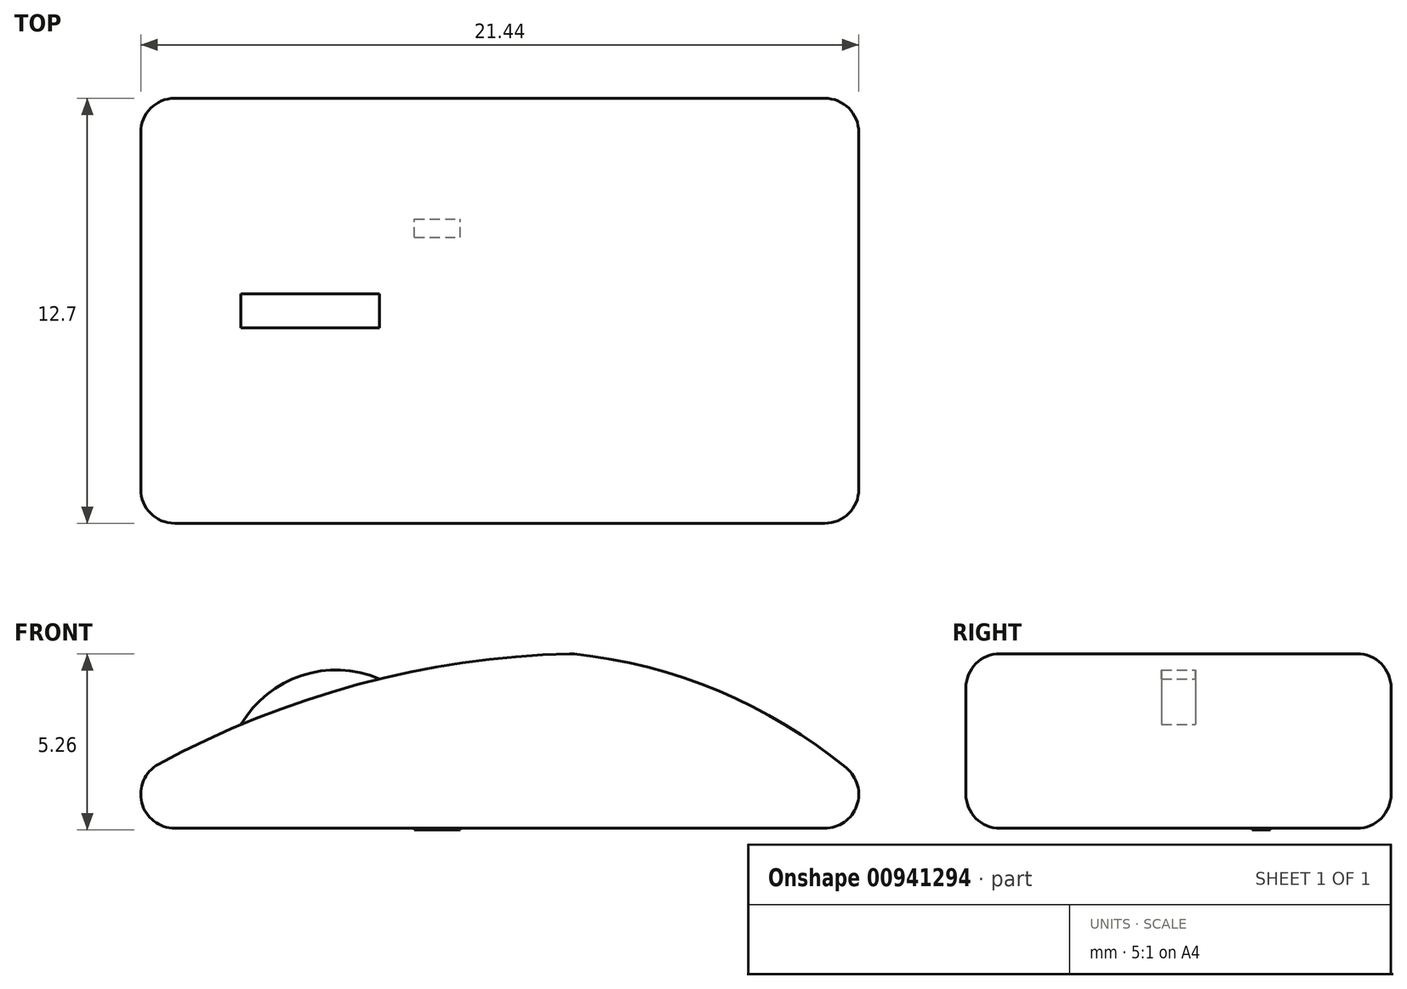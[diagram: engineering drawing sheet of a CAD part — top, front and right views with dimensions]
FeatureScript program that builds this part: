
annotation { "Feature Type Name" : "Feature", "Feature Type Description" : "" }
export const myFeature = defineFeature(function(context is Context, id is Id, definition is map)
    precondition{}
    {
        {
            var Q0;
            Q0=qCreatedBy(makeId("Front.planeOp"),FACE);
            var sketch = newSketch(context, id + "F0", { "sketchPlane" : qUnion([Q0])});
            skLineSegment(sketch, "E0", {"start": v(-53.26, -21) * mm, "end": v(73.74, -21) * mm});
            skArc(sketch, "E1", {"start": v(73.74, -21) * mm, "mid": v(51.12, -3.16) * mm, "end": v(23.51, 5.07) * mm});
            skArc(sketch, "E2", {"start": v(23.51, 5.07) * mm, "mid": v(-16.87, -2.09) * mm, "end": v(-53.26, -21) * mm});
            skArc(sketch, "E3", {"start": v(-5.21, 1.3) * mm, "mid": v(-16.84, 1.81) * mm, "end": v(-25.9, -5.52) * mm});
            skSolve(sketch);
        }
        {
            var Q0;
            {var subQ5=sQuery(id+"F0.wireOp",EDGE,"E0");Q0=makeQuery(id+"F0.imprint","IMPRINT",FACE,{"disambiguationData":[TD([[makeQuery(id+"F0.imprint","IMPRINT",EDGE,{"derivedFrom":subQ5}),1.0]])]});}
            extrude(context, id + "F1", {"entities" : qUnion([Q0]), "depth" : 31.75 * mm, "offsetDistance" : 25.4 * mm, "hasSecondDirection" : true, "secondDirectionOppositeDirection" : true, "secondDirectionDepth" : 31.75 * mm});
        }
        {
            var Q0;
            {var subQ0=sQuery(id+"F0.wireOp",EDGE,"E3");Q0=makeQuery(id+"F0.imprint","IMPRINT",FACE,{"disambiguationData":[TD([[makeQuery(id+"F0.imprint","IMPRINT",EDGE,{"derivedFrom":subQ0}),1.0]])]});}
            extrude(context, id + "F2", {"entities" : qUnion([Q0]), "operationType" : NewBodyOperationType.ADD, "depth" : 2.54 * mm, "offsetDistance" : 25.4 * mm, "hasSecondDirection" : true, "secondDirectionOppositeDirection" : true, "secondDirectionDepth" : 2.54 * mm});
        }
        {
            var Q0;
            Q0=makeQuery(id+"F1.opExtrude","SWEPT_EDGE",EDGE,{"disambiguationData":[OSD([sQuery(id+"F0.wireOp",EDGE,"E0"),sQuery(id+"F0.wireOp",EDGE,"E2")])]});
            var Q1;
            Q1=makeQuery(id+"F1.opExtrude","CAP_FACE",FACE,{"disambiguationData":[OSD([sQuery(id+"F0.wireOp",EDGE,"E0"),sQuery(id+"F0.wireOp",EDGE,"E1"),sQuery(id+"F0.wireOp",EDGE,"E2")])],"isStart":false});
            var Q2;
            Q2=makeQuery(id+"F1.opExtrude","CAP_FACE",FACE,{"disambiguationData":[OSD([sQuery(id+"F0.wireOp",EDGE,"E0"),sQuery(id+"F0.wireOp",EDGE,"E1"),sQuery(id+"F0.wireOp",EDGE,"E2")])],"isStart":true});
            var Q3;
            Q3=makeQuery(id+"F1.opExtrude","SWEPT_FACE",FACE,{"disambiguationData":[OSD([sQuery(id+"F0.wireOp",EDGE,"E1")])]});
            var Q4;
            Q4=makeQuery(id+"F1.opExtrude","SWEPT_EDGE",EDGE,{"disambiguationData":[OSD([sQuery(id+"F0.wireOp",EDGE,"E1"),sQuery(id+"F0.wireOp",EDGE,"E2")])]});
            fillet(context, id + "F3", {"entities" : qUnion([Q0, Q1, Q2, Q3, Q4]), "radius" : 5.08 * mm, "tangentPropagation" : true, "allowEdgeOverflow" : false});
        }
        {
            var Q0;
            Q0=makeQuery(id+"F1.opExtrude","SWEPT_FACE",FACE,{"disambiguationData":[OSD([sQuery(id+"F0.wireOp",EDGE,"E0")])]});
            var sketch = newSketch(context, id + "F4", { "sketchPlane" : qUnion([Q0])});
            skLineSegment(sketch, "E4.bottom", {"start": v(-35.73, -2.91) * mm, "end": v(-17.73, -2.91) * mm});
            skLineSegment(sketch, "E4.top", {"start": v(-35.73, 2.9) * mm, "end": v(-17.73, 2.9) * mm});
            skLineSegment(sketch, "E4.left", {"start": v(-35.73, -2.91) * mm, "end": v(-35.73, 2.9) * mm});
            skLineSegment(sketch, "E4.right", {"start": v(-17.73, -2.91) * mm, "end": v(-17.73, 2.9) * mm});
            skLineSegment(sketch, "E5.bottom", {"start": v(-17.73, 0) * mm, "end": v(-1.12, 0) * mm});
            skLineSegment(sketch, "E5.top", {"start": v(-17.73, 0) * mm, "end": v(-1.12, 0) * mm});
            skLineSegment(sketch, "E5.left", {"start": v(-17.73, 0) * mm, "end": v(-17.73, 0) * mm});
            skLineSegment(sketch, "E5.right", {"start": v(-1.12, 0) * mm, "end": v(-1.12, 0) * mm});
            skLineSegment(sketch, "E6.bottom", {"start": v(-35.73, 0) * mm, "end": v(-48.83, 0) * mm});
            skLineSegment(sketch, "E6.top", {"start": v(-35.73, 0) * mm, "end": v(-48.83, 0) * mm});
            skLineSegment(sketch, "E6.left", {"start": v(-35.73, 0) * mm, "end": v(-35.73, 0) * mm});
            skLineSegment(sketch, "E6.right", {"start": v(-48.83, 0) * mm, "end": v(-48.83, 0) * mm});
            skSolve(sketch);
        }
        {
            var Q0;
            {var subQ3=sQuery(id+"F4.wireOp",EDGE,"E4.bottom");Q0=makeQuery(id+"F4.imprint","IMPRINT",FACE,{"disambiguationData":[TD([[makeQuery(id+"F4.imprint","IMPRINT",EDGE,{"derivedFrom":subQ3}),-1.0]])]});}
            var sketch = newSketch(context, id + "F5", { "sketchPlane" : qUnion([Q0])});
            skLineSegment(sketch, "E7.bottom", {"start": v(0, -11) * mm, "end": v(6.83, -11) * mm});
            skLineSegment(sketch, "E7.top", {"start": v(0, -13.71) * mm, "end": v(6.83, -13.71) * mm});
            skLineSegment(sketch, "E7.left", {"start": v(0, -11) * mm, "end": v(0, -13.71) * mm});
            skLineSegment(sketch, "E7.right", {"start": v(6.83, -11) * mm, "end": v(6.83, -13.71) * mm});
            skSolve(sketch);
        }
        {
            var Q0;
            Q0=makeQuery(id+"F5.imprint","IMPRINT",FACE,{"disambiguationData":[TD([[makeQuery(id+"F5.imprint","IMPRINT",EDGE,{"derivedFrom":sQuery(id+"F5.wireOp",EDGE,"E7.bottom")}),-1.0]])]});
            extrude(context, id + "F6", {"entities" : qUnion([Q0]), "operationType" : NewBodyOperationType.ADD, "depth" : 0.25 * mm, "offsetDistance" : 25.4 * mm});
        }
        {
            var Q0;
            Q0=makeQuery(id+"F1.opExtrude","SWEPT_BODY",BODY,{"disambiguationData":[OSD([sQuery(id+"F0.wireOp",EDGE,"E0"),sQuery(id+"F0.wireOp",EDGE,"E1"),sQuery(id+"F0.wireOp",EDGE,"E2")])]});
            var Q1;
            Q1=qCreatedBy(makeId("Origin.pointOp"),VERTEX);
            transform(context, id + "F7", {"entities" : qUnion([Q0]), "transformType" : TransformType.SCALE_UNIFORMLY, "scale" : 1 / 5, "scalePoint" : qUnion([Q1]), "makeCopy" : false});
        }
    });
